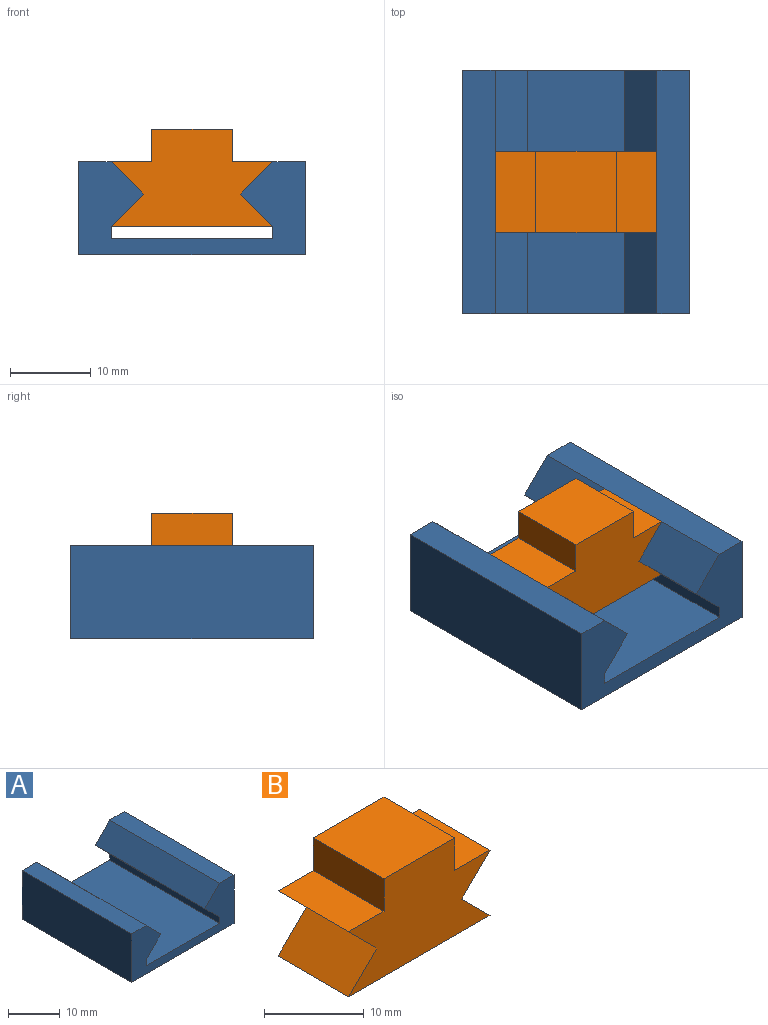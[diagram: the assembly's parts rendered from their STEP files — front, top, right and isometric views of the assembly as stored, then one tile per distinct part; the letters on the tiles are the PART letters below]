
ASSEMBLY  parts=2 mates=1
PART A: 14 faces, bbox 28x30x11.5 mm
  f0: plane 30x1.5mm, normal (1,0,0), area 45mm2, adj f1,f6,f7,f8
  f1: plane 30x4mm, normal (0.71,0,-0.71), area 169.7mm2, adj f0,f2,f7,f8
  f2: plane 30x4mm, normal (0.71,0,0.71), area 169.7mm2, adj f1,f3,f7,f8
  f3: plane 30x4mm, normal (0,0,1), area 120mm2, adj f2,f4,f7,f8
  f4: plane 30x11.5mm, normal (-1,0,0), area 345mm2, adj f3,f5,f7,f8
  f5: plane 30x28mm, normal (0,0,-1), area 840mm2, adj f4,f7,f8,f13
  f6: plane 30x20mm, normal (0,0,1), area 600mm2, adj f0,f7,f8,f9
  f7: plane 28x11.5mm, normal (0,-1,0), area 164mm2, adj f0,f1,f2,f3,f4,f5,f6,f9
  f8: plane 28x11.5mm, normal (0,1,0), area 164mm2, adj f0,f1,f2,f3,f4,f5,f6,f9
  f9: plane 30x1.5mm, normal (-1,0,0), area 45mm2, adj f6,f7,f8,f10
  f10: plane 30x4mm, normal (-0.71,0,-0.71), area 169.7mm2, adj f7,f8,f9,f11
  f11: plane 30x4mm, normal (-0.71,0,0.71), area 169.7mm2, adj f7,f8,f10,f12
  f12: plane 30x4mm, normal (0,0,1), area 120mm2, adj f7,f8,f11,f13
  f13: plane 30x11.5mm, normal (1,0,0), area 345mm2, adj f5,f7,f8,f12
PART B: 12 faces, bbox 20x10x12 mm
  f0: plane 10x4mm, normal (-1,0,0), area 40mm2, adj f1,f5,f6,f7
  f1: plane 10x5mm, normal (0,0,1), area 50mm2, adj f0,f2,f6,f7
  f2: plane 10x4mm, normal (-0.71,0,-0.71), area 56.6mm2, adj f1,f3,f6,f7
  f3: plane 10x4mm, normal (-0.71,0,0.71), area 56.6mm2, adj f2,f4,f6,f7
  f4: plane 20x10mm, normal (0,0,-1), area 200mm2, adj f3,f6,f7,f11
  f5: plane 10x10mm, normal (0,0,1), area 100mm2, adj f0,f6,f7,f8
  f6: plane 20x12mm, normal (0,-1,0), area 168mm2, adj f0,f1,f2,f3,f4,f5,f8,f9
  f7: plane 20x12mm, normal (0,1,0), area 168mm2, adj f0,f1,f2,f3,f4,f5,f8,f9
  f8: plane 10x4mm, normal (1,0,0), area 40mm2, adj f5,f6,f7,f9
  f9: plane 10x5mm, normal (0,0,1), area 50mm2, adj f6,f7,f8,f10
  f10: plane 10x4mm, normal (0.71,0,-0.71), area 56.6mm2, adj f6,f7,f9,f11
  f11: plane 10x4mm, normal (0.71,0,0.71), area 56.6mm2, adj f4,f6,f7,f10
PLACE A t=(-14.19,6.07,-4.87)mm fixed
PLACE B t=(-14.19,-3.93,-3.37)mm
MATE planar B.f2 <-> A.f2  axis (-0.71,0,-0.71) through (-22.19,-8.93,2.63)mm
